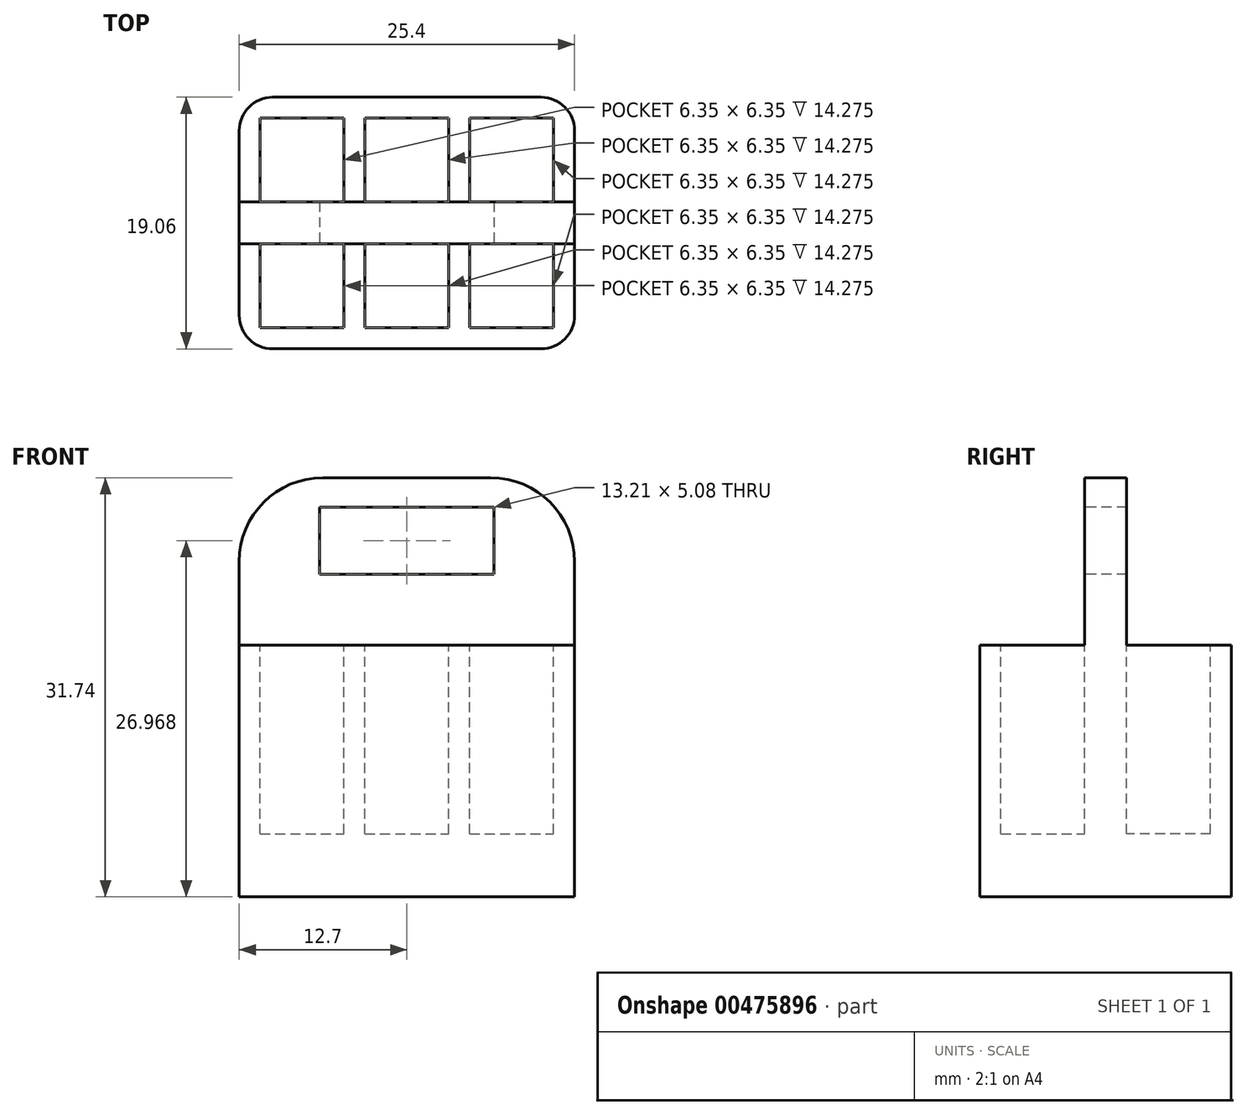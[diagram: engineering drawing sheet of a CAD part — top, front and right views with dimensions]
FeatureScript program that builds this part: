
annotation { "Feature Type Name" : "Feature", "Feature Type Description" : "" }
export const myFeature = defineFeature(function(context is Context, id is Id, definition is map)
    precondition{}
    {
        {
            var Q0;
            Q0=qCreatedBy(makeId("Right.planeOp"),FACE);
            var sketch = newSketch(context, id + "F0", { "sketchPlane" : qUnion([Q0])});
            skLineSegment(sketch, "E0.bottom", {"start": v(9.53, 9.52) * mm, "end": v(-9.53, 9.52) * mm});
            skLineSegment(sketch, "E0.top", {"start": v(9.53, -9.53) * mm, "end": v(-9.52, -9.53) * mm});
            skLineSegment(sketch, "E0.left", {"start": v(9.53, 9.53) * mm, "end": v(9.53, -9.53) * mm});
            skLineSegment(sketch, "E0.right", {"start": v(-9.53, 9.53) * mm, "end": v(-9.52, -9.53) * mm});
            skPoint(sketch, "E0.middle", {"position": v(0, 0) * mm});
            skLineSegment(sketch, "E1.bottom", {"start": v(1.59, 22.2) * mm, "end": v(-1.59, 22.2) * mm});
            skLineSegment(sketch, "E1.top", {"start": v(1.59, 9.5) * mm, "end": v(-1.59, 9.5) * mm});
            skLineSegment(sketch, "E1.left", {"start": v(1.59, 22.2) * mm, "end": v(1.59, 9.5) * mm});
            skLineSegment(sketch, "E1.right", {"start": v(-1.59, 22.2) * mm, "end": v(-1.59, 9.5) * mm});
            skPoint(sketch, "E1.middle", {"position": v(0, 15.86) * mm});
            skSolve(sketch);
        }
        {
            var Q0;
            Q0 = qSketchRegion(id + "F0", true);
            extrude(context, id + "F1", {"entities" : qUnion([Q0]), "depth" : 25.4 * mm});
        }
        {
            var Q0;
            Q0=makeQuery(id+"F1.opExtrude","CAP_EDGE",EDGE,{"disambiguationData":[OSD([sQuery(id+"F0.wireOp",EDGE,"E1.bottom")])],"isStart":false});
            var Q1;
            Q1=makeQuery(id+"F1.opExtrude","CAP_EDGE",EDGE,{"disambiguationData":[OSD([sQuery(id+"F0.wireOp",EDGE,"E1.bottom")])],"isStart":true});
            fillet(context, id + "F2", {"entities" : qUnion([Q0, Q1]), "radius" : 6.35 * mm, "tangentPropagation" : true, "allowEdgeOverflow" : false});
        }
        {
            var Q0;
            Q0=qCreatedBy(makeId("Front.planeOp"),FACE);
            var sketch = newSketch(context, id + "F3", { "sketchPlane" : qUnion([Q0])});
            skLineSegment(sketch, "E2.bottom", {"start": v(6.1, 19.98) * mm, "end": v(19.3, 19.98) * mm});
            skLineSegment(sketch, "E2.top", {"start": v(6.1, 14.9) * mm, "end": v(19.3, 14.9) * mm});
            skLineSegment(sketch, "E2.left", {"start": v(6.1, 19.98) * mm, "end": v(6.1, 14.9) * mm});
            skLineSegment(sketch, "E2.right", {"start": v(19.3, 19.98) * mm, "end": v(19.3, 14.9) * mm});
            skSolve(sketch);
        }
        {
            var Q0;
            Q0 = qSketchRegion(id + "F3", true);
            extrude(context, id + "F4", {"entities" : qUnion([Q0]), "operationType" : NewBodyOperationType.REMOVE, "endBound" : BoundingType.SYMMETRIC, "oppositeDirection" : true, "depth" : 25.4 * mm});
        }
        {
            var Q0;
            Q0=qCreatedBy(makeId("Top.planeOp"),FACE);
            var sketch = newSketch(context, id + "F5", { "sketchPlane" : qUnion([Q0])});
            skLineSegment(sketch, "E3.left", {"start": v(1.59, 7.94) * mm, "end": v(1.59, 1.59) * mm});
            skLineSegment(sketch, "E3.right", {"start": v(23.81, 7.94) * mm, "end": v(23.81, 1.59) * mm});
            skLineSegment(sketch, "E4.left", {"start": v(7.94, 7.94) * mm, "end": v(7.94, 1.59) * mm});
            skLineSegment(sketch, "E4.right", {"start": v(9.53, 7.94) * mm, "end": v(9.53, 1.59) * mm});
            skLineSegment(sketch, "E5.left", {"start": v(15.88, 7.94) * mm, "end": v(15.88, 1.59) * mm});
            skLineSegment(sketch, "E5.right", {"start": v(17.46, 7.94) * mm, "end": v(17.46, 1.59) * mm});
            skLineSegment(sketch, "E6", {"start": v(1.59, 7.94) * mm, "end": v(7.94, 7.94) * mm});
            skLineSegment(sketch, "E7", {"start": v(1.59, 1.59) * mm, "end": v(7.94, 1.59) * mm});
            skLineSegment(sketch, "E8", {"start": v(9.53, 7.94) * mm, "end": v(15.88, 7.94) * mm});
            skLineSegment(sketch, "E9", {"start": v(9.53, 1.59) * mm, "end": v(15.88, 1.59) * mm});
            skLineSegment(sketch, "E10", {"start": v(17.46, 7.94) * mm, "end": v(23.81, 7.94) * mm});
            skLineSegment(sketch, "E11", {"start": v(17.46, 1.59) * mm, "end": v(23.81, 1.59) * mm});
            skLineSegment(sketch, "E12.MirrorCS", {"start": v(1.59, -1.59) * mm, "end": v(7.94, -1.59) * mm});
            skLineSegment(sketch, "E13.MirrorCS", {"start": v(7.94, -7.94) * mm, "end": v(7.94, -1.59) * mm});
            skLineSegment(sketch, "E14.MirrorCS", {"start": v(1.59, -7.94) * mm, "end": v(1.59, -1.59) * mm});
            skLineSegment(sketch, "E15.MirrorCS", {"start": v(1.59, -7.94) * mm, "end": v(7.94, -7.94) * mm});
            skLineSegment(sketch, "E16.MirrorCS", {"start": v(9.53, -7.94) * mm, "end": v(9.53, -1.59) * mm});
            skLineSegment(sketch, "E17.MirrorCS", {"start": v(9.53, -7.94) * mm, "end": v(15.88, -7.94) * mm});
            skLineSegment(sketch, "E18.MirrorCS", {"start": v(15.88, -7.94) * mm, "end": v(15.88, -1.59) * mm});
            skLineSegment(sketch, "E19.MirrorCS", {"start": v(9.53, -1.59) * mm, "end": v(15.88, -1.59) * mm});
            skLineSegment(sketch, "E20.MirrorCS", {"start": v(17.46, -1.59) * mm, "end": v(23.81, -1.59) * mm});
            skLineSegment(sketch, "E21.MirrorCS", {"start": v(23.81, -7.94) * mm, "end": v(23.81, -1.59) * mm});
            skLineSegment(sketch, "E22.MirrorCS", {"start": v(17.46, -7.94) * mm, "end": v(23.81, -7.94) * mm});
            skLineSegment(sketch, "E23.MirrorCS", {"start": v(17.46, -7.94) * mm, "end": v(17.46, -1.59) * mm});
            skSolve(sketch);
        }
        {
            var Q0;
            Q0 = qSketchRegion(id + "F5", true);
            extrude(context, id + "F6", {"entities" : qUnion([Q0]), "operationType" : NewBodyOperationType.REMOVE, "depth" : -4.75 * mm, "hasSecondDirection" : true, "secondDirectionOppositeDirection" : false, "secondDirectionDepth" : 50.8 * mm});
        }
        {
            var Q0;
            Q0=makeQuery(id+"F1.opExtrude","CAP_EDGE",EDGE,{"disambiguationData":[OSD([sQuery(id+"F0.wireOp",EDGE,"E0.right")])],"isStart":false});
            var Q1;
            Q1=makeQuery(id+"F1.opExtrude","CAP_EDGE",EDGE,{"disambiguationData":[OSD([sQuery(id+"F0.wireOp",EDGE,"E0.right")])],"isStart":true});
            var Q2;
            Q2=makeQuery(id+"F1.opExtrude","CAP_EDGE",EDGE,{"disambiguationData":[OSD([sQuery(id+"F0.wireOp",EDGE,"E0.left")])],"isStart":false});
            var Q3;
            Q3=makeQuery(id+"F1.opExtrude","CAP_EDGE",EDGE,{"disambiguationData":[OSD([sQuery(id+"F0.wireOp",EDGE,"E0.left")])],"isStart":true});
            fillet(context, id + "F7", {"entities" : qUnion([Q0, Q1, Q2, Q3]), "radius" : 2.54 * mm, "tangentPropagation" : true, "allowEdgeOverflow" : false});
        }
    });
